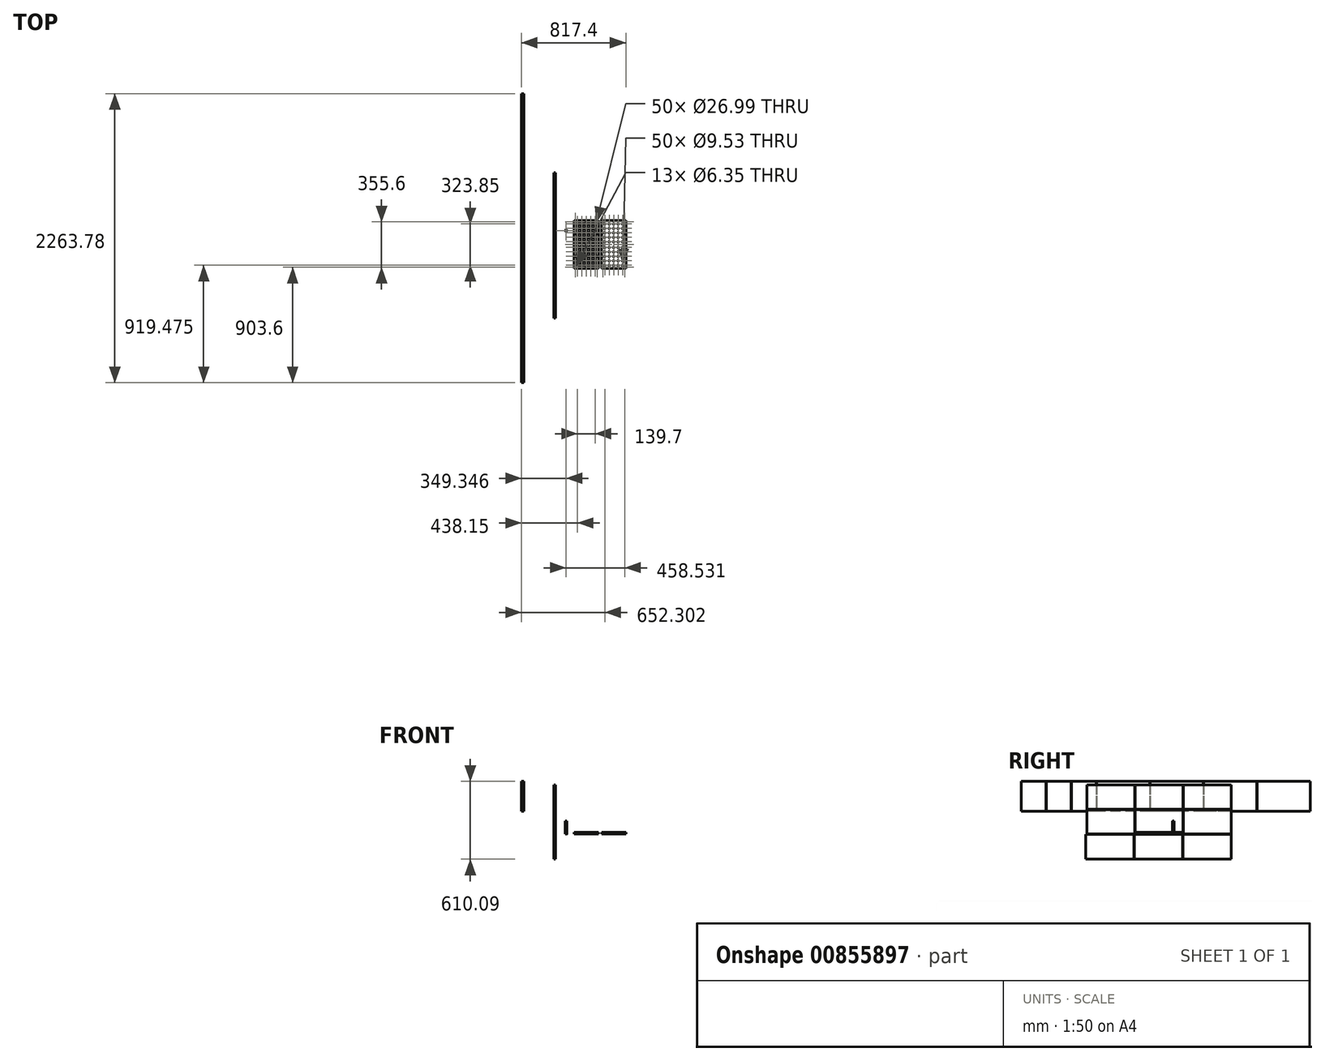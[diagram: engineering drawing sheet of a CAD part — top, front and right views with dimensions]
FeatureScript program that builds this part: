
annotation { "Feature Type Name" : "Feature", "Feature Type Description" : "" }
export const myFeature = defineFeature(function(context is Context, id is Id, definition is map)
    precondition{}
    {
        {
            var Q0;
            Q0=qCreatedBy(makeId("Top.planeOp"),FACE);
            var sketch = newSketch(context, id + "F0", { "sketchPlane" : qUnion([Q0])});
            skLineSegment(sketch, "E0.bottom", {"start": v(95.25, -187.33) * mm, "end": v(-95.25, -187.33) * mm});
            skLineSegment(sketch, "E0.top", {"start": v(95.25, 187.33) * mm, "end": v(-95.25, 187.33) * mm});
            skLineSegment(sketch, "E0.left", {"start": v(95.25, -187.33) * mm, "end": v(95.25, 187.33) * mm});
            skLineSegment(sketch, "E0.right", {"start": v(-95.25, -187.33) * mm, "end": v(-95.25, 187.33) * mm});
            skPoint(sketch, "E0.middle", {"position": v(0, 0) * mm});
            skSolve(sketch);
        }
        {
            var Q0;
            Q0=makeQuery(id+"F0.imprint","IMPRINT",FACE,{"disambiguationData":[TD([[makeQuery(id+"F0.imprint","IMPRINT",EDGE,{"derivedFrom":sQuery(id+"F0.wireOp",EDGE,"E0.bottom")}),-1.0]])]});
            extrude(context, id + "F1", {"entities" : qUnion([Q0]), "depth" : 12.7 * mm, "offsetDistance" : 25.4 * mm});
        }
        {
            var Q0;
            Q0=makeQuery(id+"F1.opExtrude","CAP_FACE",FACE,{"disambiguationData":[OSD([sQuery(id+"F0.wireOp",EDGE,"E0.bottom"),sQuery(id+"F0.wireOp",EDGE,"E0.top"),sQuery(id+"F0.wireOp",EDGE,"E0.left"),sQuery(id+"F0.wireOp",EDGE,"E0.right")])],"isStart":false});
            var sketch = newSketch(context, id + "F2", { "sketchPlane" : qUnion([Q0])});
            skLineSegment(sketch, "E1", {"start": v(-95.25, 161.92) * mm, "end": v(95.25, 161.93) * mm, "construction": true});
            skLineSegment(sketch, "E2", {"start": v(-69.85, 187.33) * mm, "end": v(-69.85, -187.33) * mm, "construction": true});
            skCircle(sketch, "E3", {"center": v(-69.85, 161.93) * mm, "radius": 13.5 * mm});
            skCircle(sketch, "E4.0.1.0", {"center": v(-69.85, 127) * mm, "radius": 13.5 * mm});
            skCircle(sketch, "E4.0.2.0", {"center": v(-69.85, 92.08) * mm, "radius": 13.5 * mm});
            skCircle(sketch, "E4.0.3.0", {"center": v(-69.85, 57.15) * mm, "radius": 13.5 * mm});
            skCircle(sketch, "E4.0.4.0", {"center": v(-69.85, 22.22) * mm, "radius": 13.5 * mm});
            skCircle(sketch, "E4.1.0.0", {"center": v(-34.93, 161.93) * mm, "radius": 13.5 * mm});
            skCircle(sketch, "E4.1.1.0", {"center": v(-34.93, 127) * mm, "radius": 13.5 * mm});
            skCircle(sketch, "E4.1.2.0", {"center": v(-34.93, 92.08) * mm, "radius": 13.5 * mm});
            skCircle(sketch, "E4.1.3.0", {"center": v(-34.93, 57.15) * mm, "radius": 13.5 * mm});
            skCircle(sketch, "E4.1.4.0", {"center": v(-34.93, 22.22) * mm, "radius": 13.5 * mm});
            skCircle(sketch, "E4.2.0.0", {"center": v(0, 161.93) * mm, "radius": 13.5 * mm});
            skCircle(sketch, "E4.2.1.0", {"center": v(0, 127) * mm, "radius": 13.5 * mm});
            skCircle(sketch, "E4.2.2.0", {"center": v(0, 92.08) * mm, "radius": 13.5 * mm});
            skCircle(sketch, "E4.2.3.0", {"center": v(0, 57.15) * mm, "radius": 13.5 * mm});
            skCircle(sketch, "E4.2.4.0", {"center": v(0, 22.22) * mm, "radius": 13.5 * mm});
            skCircle(sketch, "E4.3.0.0", {"center": v(34.92, 161.93) * mm, "radius": 13.5 * mm});
            skCircle(sketch, "E4.3.1.0", {"center": v(34.92, 127) * mm, "radius": 13.5 * mm});
            skCircle(sketch, "E4.3.2.0", {"center": v(34.92, 92.08) * mm, "radius": 13.5 * mm});
            skCircle(sketch, "E4.3.3.0", {"center": v(34.92, 57.15) * mm, "radius": 13.5 * mm});
            skCircle(sketch, "E4.3.4.0", {"center": v(34.92, 22.22) * mm, "radius": 13.5 * mm});
            skCircle(sketch, "E4.4.0.0", {"center": v(69.85, 161.93) * mm, "radius": 13.5 * mm});
            skCircle(sketch, "E4.4.1.0", {"center": v(69.85, 127) * mm, "radius": 13.5 * mm});
            skCircle(sketch, "E4.4.2.0", {"center": v(69.85, 92.08) * mm, "radius": 13.5 * mm});
            skCircle(sketch, "E4.4.3.0", {"center": v(69.85, 57.15) * mm, "radius": 13.5 * mm});
            skCircle(sketch, "E4.4.4.0", {"center": v(69.85, 22.22) * mm, "radius": 13.5 * mm});
            skLineSegment(sketch, "E4.direction1", {"start": v(-69.85, 161.93) * mm, "end": v(-34.93, 161.93) * mm, "construction": true});
            skLineSegment(sketch, "E4.direction2", {"start": v(-69.85, 161.93) * mm, "end": v(-69.85, 127) * mm, "construction": true});
            skLineSegment(sketch, "E5", {"start": v(-95.25, -161.93) * mm, "end": v(95.25, -161.92) * mm, "construction": true});
            skCircle(sketch, "E6", {"center": v(-69.85, -161.93) * mm, "radius": 13.5 * mm});
            skLineSegment(sketch, "E7", {"start": v(95.25, -177.8) * mm, "end": v(-95.25, -177.8) * mm, "construction": true});
            skLineSegment(sketch, "E8", {"start": v(85.73, -187.33) * mm, "end": v(85.73, 187.33) * mm, "construction": true});
            skLineSegment(sketch, "E9", {"start": v(-95.25, 0) * mm, "end": v(95.25, 0) * mm, "construction": true});
            skLineSegment(sketch, "E10", {"start": v(-95.25, 177.8) * mm, "end": v(95.25, 177.8) * mm, "construction": true});
            skLineSegment(sketch, "E11", {"start": v(-85.73, 187.33) * mm, "end": v(-85.72, -187.33) * mm, "construction": true});
            skCircle(sketch, "E12", {"center": v(-85.73, 177.8) * mm, "radius": 3.18 * mm});
            skCircle(sketch, "E13", {"center": v(85.73, 177.8) * mm, "radius": 3.18 * mm});
            skCircle(sketch, "E14", {"center": v(-85.73, 0) * mm, "radius": 3.18 * mm});
            skCircle(sketch, "E15", {"center": v(85.73, 0) * mm, "radius": 3.18 * mm});
            skCircle(sketch, "E16", {"center": v(-85.72, -177.8) * mm, "radius": 3.18 * mm});
            skCircle(sketch, "E17", {"center": v(85.73, -177.8) * mm, "radius": 3.18 * mm});
            skCircle(sketch, "E18.0.1.0", {"center": v(-69.85, -127) * mm, "radius": 13.5 * mm});
            skCircle(sketch, "E18.0.2.0", {"center": v(-69.85, -92.08) * mm, "radius": 13.5 * mm});
            skCircle(sketch, "E18.0.3.0", {"center": v(-69.85, -57.15) * mm, "radius": 13.5 * mm});
            skCircle(sketch, "E18.0.4.0", {"center": v(-69.85, -22.23) * mm, "radius": 13.5 * mm});
            skCircle(sketch, "E18.1.0.0", {"center": v(-34.93, -161.93) * mm, "radius": 13.5 * mm});
            skCircle(sketch, "E18.1.1.0", {"center": v(-34.93, -127) * mm, "radius": 13.5 * mm});
            skCircle(sketch, "E18.1.2.0", {"center": v(-34.93, -92.08) * mm, "radius": 13.5 * mm});
            skCircle(sketch, "E18.1.3.0", {"center": v(-34.93, -57.15) * mm, "radius": 13.5 * mm});
            skCircle(sketch, "E18.1.4.0", {"center": v(-34.93, -22.23) * mm, "radius": 13.5 * mm});
            skCircle(sketch, "E18.2.0.0", {"center": v(0, -161.93) * mm, "radius": 13.5 * mm});
            skCircle(sketch, "E18.2.1.0", {"center": v(0, -127) * mm, "radius": 13.5 * mm});
            skCircle(sketch, "E18.2.2.0", {"center": v(0, -92.08) * mm, "radius": 13.5 * mm});
            skCircle(sketch, "E18.2.3.0", {"center": v(0, -57.15) * mm, "radius": 13.5 * mm});
            skCircle(sketch, "E18.2.4.0", {"center": v(0, -22.23) * mm, "radius": 13.5 * mm});
            skCircle(sketch, "E18.3.0.0", {"center": v(34.92, -161.93) * mm, "radius": 13.5 * mm});
            skCircle(sketch, "E18.3.1.0", {"center": v(34.92, -127) * mm, "radius": 13.5 * mm});
            skCircle(sketch, "E18.3.2.0", {"center": v(34.92, -92.08) * mm, "radius": 13.5 * mm});
            skCircle(sketch, "E18.3.3.0", {"center": v(34.92, -57.15) * mm, "radius": 13.5 * mm});
            skCircle(sketch, "E18.3.4.0", {"center": v(34.92, -22.23) * mm, "radius": 13.5 * mm});
            skCircle(sketch, "E18.4.0.0", {"center": v(69.85, -161.93) * mm, "radius": 13.5 * mm});
            skCircle(sketch, "E18.4.1.0", {"center": v(69.85, -127) * mm, "radius": 13.5 * mm});
            skCircle(sketch, "E18.4.2.0", {"center": v(69.85, -92.08) * mm, "radius": 13.5 * mm});
            skCircle(sketch, "E18.4.3.0", {"center": v(69.85, -57.15) * mm, "radius": 13.5 * mm});
            skCircle(sketch, "E18.4.4.0", {"center": v(69.85, -22.23) * mm, "radius": 13.5 * mm});
            skLineSegment(sketch, "E18.direction1", {"start": v(-69.85, -161.93) * mm, "end": v(-34.93, -161.93) * mm, "construction": true});
            skLineSegment(sketch, "E18.direction2", {"start": v(-69.85, -161.93) * mm, "end": v(-69.85, -127) * mm, "construction": true});
            skSolve(sketch);
        }
        {
            var Q0;
            Q0 = qSketchRegion(id + "F2", true);
            extrude(context, id + "F3", {"entities" : qUnion([Q0]), "operationType" : NewBodyOperationType.REMOVE, "endBound" : BoundingType.UP_TO_NEXT, "oppositeDirection" : true, "depth" : 25.4 * mm, "offsetDistance" : 25.4 * mm});
        }
        {
            var Q0;
            Q0=qCreatedBy(makeId("Top.planeOp"),FACE);
            var sketch = newSketch(context, id + "F4", { "sketchPlane" : qUnion([Q0])});
            skCircle(sketch, "E19", {"center": v(-158.65, 110) * mm, "radius": 6.35 * mm});
            skCircle(sketch, "E20", {"center": v(-158.65, 110) * mm, "radius": 3.18 * mm});
            skSolve(sketch);
        }
        {
            var Q0;
            Q0=makeQuery(id+"F4.imprint","IMPRINT",FACE,{"disambiguationData":[TD([[makeQuery(id+"F4.imprint","IMPRINT",EDGE,{"derivedFrom":sQuery(id+"F4.wireOp",EDGE,"E19")}),1.0]])]});
            extrude(context, id + "F5", {"entities" : qUnion([Q0]), "depth" : 101.6 * mm, "offsetDistance" : 25.4 * mm});
        }
        {
            var Q0;
            Q0=qCreatedBy(makeId("Top.planeOp"),FACE);
            var sketch = newSketch(context, id + "F6", { "sketchPlane" : qUnion([Q0])});
            skLineSegment(sketch, "E21.bottom", {"start": v(118.9, 187.33) * mm, "end": v(309.4, 187.33) * mm});
            skLineSegment(sketch, "E21.top", {"start": v(118.9, -187.33) * mm, "end": v(309.4, -187.33) * mm});
            skLineSegment(sketch, "E21.left", {"start": v(118.9, 187.33) * mm, "end": v(118.9, -187.33) * mm});
            skLineSegment(sketch, "E21.right", {"start": v(309.4, 187.33) * mm, "end": v(309.4, -187.33) * mm});
            skPoint(sketch, "E21.middle", {"position": v(214.15, 0) * mm});
            skSolve(sketch);
        }
        {
            var Q0;
            Q0=makeQuery(id+"F6.imprint","IMPRINT",FACE,{"disambiguationData":[TD([[makeQuery(id+"F6.imprint","IMPRINT",EDGE,{"derivedFrom":sQuery(id+"F6.wireOp",EDGE,"E21.bottom")}),-1.0]])]});
            extrude(context, id + "F7", {"entities" : qUnion([Q0]), "depth" : 12.7 * mm, "offsetDistance" : 25.4 * mm});
        }
        {
            var Q0;
            Q0=makeQuery(id+"F7.opExtrude","CAP_FACE",FACE,{"disambiguationData":[OSD([sQuery(id+"F6.wireOp",EDGE,"E21.bottom"),sQuery(id+"F6.wireOp",EDGE,"E21.top"),sQuery(id+"F6.wireOp",EDGE,"E21.left"),sQuery(id+"F6.wireOp",EDGE,"E21.right")])],"isStart":false});
            var sketch = newSketch(context, id + "F8", { "sketchPlane" : qUnion([Q0])});
            skLineSegment(sketch, "E22", {"start": v(118.9, 177.8) * mm, "end": v(309.4, 177.8) * mm, "construction": true});
            skLineSegment(sketch, "E23", {"start": v(118.9, -177.8) * mm, "end": v(309.4, -177.8) * mm, "construction": true});
            skLineSegment(sketch, "E24", {"start": v(128.43, 187.33) * mm, "end": v(128.43, -187.33) * mm, "construction": true});
            skLineSegment(sketch, "E25", {"start": v(299.88, 187.33) * mm, "end": v(299.88, -187.33) * mm, "construction": true});
            skLineSegment(sketch, "E26", {"start": v(118.9, 0) * mm, "end": v(309.4, 0) * mm, "construction": true});
            skCircle(sketch, "E27", {"center": v(128.43, 177.8) * mm, "radius": 3.18 * mm});
            skCircle(sketch, "E28", {"center": v(299.88, 177.8) * mm, "radius": 3.18 * mm});
            skCircle(sketch, "E29", {"center": v(128.43, 0) * mm, "radius": 3.18 * mm});
            skCircle(sketch, "E30", {"center": v(299.88, 0) * mm, "radius": 3.18 * mm});
            skCircle(sketch, "E31", {"center": v(128.43, -177.8) * mm, "radius": 3.17 * mm});
            skCircle(sketch, "E32", {"center": v(299.88, -177.8) * mm, "radius": 3.18 * mm});
            skSolve(sketch);
        }
        {
            var Q0;
            Q0 = qSketchRegion(id + "F8", true);
            extrude(context, id + "F9", {"entities" : qUnion([Q0]), "operationType" : NewBodyOperationType.REMOVE, "oppositeDirection" : true, "depth" : 25.4 * mm, "offsetDistance" : 25.4 * mm});
        }
        {
            var Q0;
            Q0=makeQuery(id+"F7.opExtrude","CAP_FACE",FACE,{"disambiguationData":[OSD([sQuery(id+"F6.wireOp",EDGE,"E21.bottom"),sQuery(id+"F6.wireOp",EDGE,"E21.top"),sQuery(id+"F6.wireOp",EDGE,"E21.left"),sQuery(id+"F6.wireOp",EDGE,"E21.right")])],"isStart":false});
            var sketch = newSketch(context, id + "F10", { "sketchPlane" : qUnion([Q0])});
            skLineSegment(sketch, "E33", {"start": v(144.3, 187.33) * mm, "end": v(144.3, -187.33) * mm, "construction": true});
            skLineSegment(sketch, "E34", {"start": v(118.9, 161.93) * mm, "end": v(309.4, 161.93) * mm, "construction": true});
            skLineSegment(sketch, "E35", {"start": v(118.9, -161.92) * mm, "end": v(309.4, -161.92) * mm, "construction": true});
            skCircle(sketch, "E36", {"center": v(144.3, 161.92) * mm, "radius": 4.76 * mm});
            skCircle(sketch, "E37.0.1.0", {"center": v(144.3, 127) * mm, "radius": 4.76 * mm});
            skCircle(sketch, "E37.0.2.0", {"center": v(144.3, 92.07) * mm, "radius": 4.76 * mm});
            skCircle(sketch, "E37.0.3.0", {"center": v(144.3, 57.15) * mm, "radius": 4.76 * mm});
            skCircle(sketch, "E37.0.4.0", {"center": v(144.3, 22.22) * mm, "radius": 4.76 * mm});
            skCircle(sketch, "E37.1.0.0", {"center": v(179.23, 161.92) * mm, "radius": 4.76 * mm});
            skCircle(sketch, "E37.1.1.0", {"center": v(179.23, 127) * mm, "radius": 4.76 * mm});
            skCircle(sketch, "E37.1.2.0", {"center": v(179.23, 92.07) * mm, "radius": 4.76 * mm});
            skCircle(sketch, "E37.1.3.0", {"center": v(179.23, 57.15) * mm, "radius": 4.76 * mm});
            skCircle(sketch, "E37.1.4.0", {"center": v(179.23, 22.22) * mm, "radius": 4.76 * mm});
            skCircle(sketch, "E37.2.0.0", {"center": v(214.15, 161.92) * mm, "radius": 4.76 * mm});
            skCircle(sketch, "E37.2.1.0", {"center": v(214.15, 127) * mm, "radius": 4.76 * mm});
            skCircle(sketch, "E37.2.2.0", {"center": v(214.15, 92.07) * mm, "radius": 4.76 * mm});
            skCircle(sketch, "E37.2.3.0", {"center": v(214.15, 57.15) * mm, "radius": 4.76 * mm});
            skCircle(sketch, "E37.2.4.0", {"center": v(214.15, 22.22) * mm, "radius": 4.76 * mm});
            skCircle(sketch, "E37.3.0.0", {"center": v(249.08, 161.92) * mm, "radius": 4.76 * mm});
            skCircle(sketch, "E37.3.1.0", {"center": v(249.08, 127) * mm, "radius": 4.76 * mm});
            skCircle(sketch, "E37.3.2.0", {"center": v(249.08, 92.07) * mm, "radius": 4.76 * mm});
            skCircle(sketch, "E37.3.3.0", {"center": v(249.08, 57.15) * mm, "radius": 4.76 * mm});
            skCircle(sketch, "E37.3.4.0", {"center": v(249.08, 22.22) * mm, "radius": 4.76 * mm});
            skCircle(sketch, "E37.4.0.0", {"center": v(284, 161.92) * mm, "radius": 4.76 * mm});
            skCircle(sketch, "E37.4.1.0", {"center": v(284, 127) * mm, "radius": 4.76 * mm});
            skCircle(sketch, "E37.4.2.0", {"center": v(284, 92.07) * mm, "radius": 4.76 * mm});
            skCircle(sketch, "E37.4.3.0", {"center": v(284, 57.15) * mm, "radius": 4.76 * mm});
            skCircle(sketch, "E37.4.4.0", {"center": v(284, 22.22) * mm, "radius": 4.76 * mm});
            skLineSegment(sketch, "E37.direction1", {"start": v(144.3, 161.93) * mm, "end": v(179.23, 161.93) * mm, "construction": true});
            skLineSegment(sketch, "E37.direction2", {"start": v(144.3, 161.92) * mm, "end": v(144.3, 127) * mm, "construction": true});
            skCircle(sketch, "E38", {"center": v(144.3, -161.92) * mm, "radius": 4.76 * mm});
            skCircle(sketch, "E39.0.1.0", {"center": v(144.3, -127) * mm, "radius": 4.76 * mm});
            skCircle(sketch, "E39.0.2.0", {"center": v(144.3, -92.07) * mm, "radius": 4.76 * mm});
            skCircle(sketch, "E39.0.3.0", {"center": v(144.3, -57.15) * mm, "radius": 4.76 * mm});
            skCircle(sketch, "E39.0.4.0", {"center": v(144.3, -22.22) * mm, "radius": 4.76 * mm});
            skCircle(sketch, "E39.1.0.0", {"center": v(179.23, -161.92) * mm, "radius": 4.76 * mm});
            skCircle(sketch, "E39.1.1.0", {"center": v(179.23, -127) * mm, "radius": 4.76 * mm});
            skCircle(sketch, "E39.1.2.0", {"center": v(179.23, -92.07) * mm, "radius": 4.76 * mm});
            skCircle(sketch, "E39.1.3.0", {"center": v(179.23, -57.15) * mm, "radius": 4.76 * mm});
            skCircle(sketch, "E39.1.4.0", {"center": v(179.23, -22.22) * mm, "radius": 4.76 * mm});
            skCircle(sketch, "E39.2.0.0", {"center": v(214.15, -161.92) * mm, "radius": 4.76 * mm});
            skCircle(sketch, "E39.2.1.0", {"center": v(214.15, -127) * mm, "radius": 4.76 * mm});
            skCircle(sketch, "E39.2.2.0", {"center": v(214.15, -92.07) * mm, "radius": 4.76 * mm});
            skCircle(sketch, "E39.2.3.0", {"center": v(214.15, -57.15) * mm, "radius": 4.76 * mm});
            skCircle(sketch, "E39.2.4.0", {"center": v(214.15, -22.22) * mm, "radius": 4.76 * mm});
            skCircle(sketch, "E39.3.0.0", {"center": v(249.08, -161.92) * mm, "radius": 4.76 * mm});
            skCircle(sketch, "E39.3.1.0", {"center": v(249.08, -127) * mm, "radius": 4.76 * mm});
            skCircle(sketch, "E39.3.2.0", {"center": v(249.08, -92.07) * mm, "radius": 4.76 * mm});
            skCircle(sketch, "E39.3.3.0", {"center": v(249.08, -57.15) * mm, "radius": 4.76 * mm});
            skCircle(sketch, "E39.3.4.0", {"center": v(249.08, -22.22) * mm, "radius": 4.76 * mm});
            skCircle(sketch, "E39.4.0.0", {"center": v(284, -161.92) * mm, "radius": 4.76 * mm});
            skCircle(sketch, "E39.4.1.0", {"center": v(284, -127) * mm, "radius": 4.76 * mm});
            skCircle(sketch, "E39.4.2.0", {"center": v(284, -92.07) * mm, "radius": 4.76 * mm});
            skCircle(sketch, "E39.4.3.0", {"center": v(284, -57.15) * mm, "radius": 4.76 * mm});
            skCircle(sketch, "E39.4.4.0", {"center": v(284, -22.22) * mm, "radius": 4.76 * mm});
            skLineSegment(sketch, "E39.direction1", {"start": v(144.3, -161.92) * mm, "end": v(179.23, -161.92) * mm, "construction": true});
            skLineSegment(sketch, "E39.direction2", {"start": v(144.3, -161.92) * mm, "end": v(144.3, -127) * mm, "construction": true});
            skSolve(sketch);
        }
        {
            var Q0;
            Q0 = qSketchRegion(id + "F10", true);
            extrude(context, id + "F11", {"entities" : qUnion([Q0]), "operationType" : NewBodyOperationType.REMOVE, "oppositeDirection" : true, "depth" : 12.7 * mm, "offsetDistance" : 25.4 * mm});
        }
        {
            var Q0;
            Q0=qCreatedBy(makeId("Right.planeOp"),FACE);
            cPlane(context, id + "F12", {"entities" : qUnion([Q0]), "cplaneType" : CPlaneType.OFFSET, "offset" : 254 * mm, "oppositeDirection" : true, "width" : 152.4 * mm, "height" : 152.4 * mm});
        }
        {
            var Q0;
            Q0=qCreatedBy(id+"F12.planeOp",FACE);
            var sketch = newSketch(context, id + "F13", { "sketchPlane" : qUnion([Q0])});
            skLineSegment(sketch, "E40.bottom", {"start": v(-655.75, 384.17) * mm, "end": v(563.45, 384.18) * mm});
            skLineSegment(sketch, "E40.top", {"start": v(-655.75, -225.43) * mm, "end": v(563.45, -225.42) * mm});
            skLineSegment(sketch, "E40.left", {"start": v(-655.75, 384.17) * mm, "end": v(-655.75, -225.43) * mm});
            skLineSegment(sketch, "E40.right", {"start": v(563.45, 384.18) * mm, "end": v(563.45, -225.42) * mm});
            skLineSegment(sketch, "E41", {"start": v(563.45, 193.68) * mm, "end": v(-655.75, 193.67) * mm});
            skLineSegment(sketch, "E42", {"start": v(563.45, 190.5) * mm, "end": v(-655.75, 190.5) * mm});
            skLineSegment(sketch, "E43", {"start": v(563.45, 0) * mm, "end": v(-655.75, 0) * mm});
            skLineSegment(sketch, "E44", {"start": v(563.45, -3.18) * mm, "end": v(-655.75, -3.18) * mm});
            skLineSegment(sketch, "E45", {"start": v(563.45, -196.85) * mm, "end": v(-655.75, -196.85) * mm});
            skLineSegment(sketch, "E46", {"start": v(188.8, 384.18) * mm, "end": v(188.8, 0) * mm});
            skLineSegment(sketch, "E47", {"start": v(185.63, 384.18) * mm, "end": v(185.63, 0) * mm});
            skLineSegment(sketch, "E48", {"start": v(-189.02, 384.17) * mm, "end": v(-189.02, 0) * mm});
            skLineSegment(sketch, "E49", {"start": v(-192.2, 384.17) * mm, "end": v(-192.2, 0) * mm});
            skLineSegment(sketch, "E50", {"start": v(-566.85, 384.17) * mm, "end": v(-566.85, 0) * mm});
            skLineSegment(sketch, "E51", {"start": v(185.63, -3.17) * mm, "end": v(185.63, -196.85) * mm});
            skLineSegment(sketch, "E52", {"start": v(182.45, -3.17) * mm, "end": v(182.45, -196.85) * mm});
            skLineSegment(sketch, "E53", {"start": v(-195.37, -3.18) * mm, "end": v(-195.37, -196.85) * mm});
            skLineSegment(sketch, "E54", {"start": v(-198.55, -3.18) * mm, "end": v(-198.55, -196.85) * mm});
            skLineSegment(sketch, "E55", {"start": v(-576.37, -3.18) * mm, "end": v(-576.37, -196.85) * mm});
            skSolve(sketch);
        }
        {
            var Q0;
            {var subQ0=sQuery(id+"F13.wireOp",EDGE,"E52");Q0=makeQuery(id+"F13.imprint","IMPRINT",FACE,{"disambiguationData":[TD([[makeQuery(id+"F13.imprint","IMPRINT",EDGE,{"derivedFrom":subQ0}),-1.0]])]});}
            cPlane(context, id + "F14", {"entities" : qUnion([Q0]), "cplaneType" : CPlaneType.OFFSET, "offset" : 254 * mm, "oppositeDirection" : true, "width" : 152.4 * mm, "height" : 152.4 * mm});
        }
        {
            var Q0;
            Q0=qCreatedBy(id+"F14.planeOp",FACE);
            var sketch = newSketch(context, id + "F15", { "sketchPlane" : qUnion([Q0])});
            skLineSegment(sketch, "E56.bottom", {"start": v(1182.38, 413.24) * mm, "end": v(-1256.02, 413.24) * mm});
            skLineSegment(sketch, "E56.top", {"start": v(1182.38, 178.3) * mm, "end": v(-1256.02, 178.3) * mm});
            skLineSegment(sketch, "E56.left", {"start": v(1182.38, 413.24) * mm, "end": v(1182.38, 178.3) * mm});
            skLineSegment(sketch, "E56.right", {"start": v(-1256.02, 413.24) * mm, "end": v(-1256.02, 178.3) * mm});
            skLineSegment(sketch, "E57", {"start": v(766.45, 413.24) * mm, "end": v(766.45, 178.3) * mm});
            skLineSegment(sketch, "E58", {"start": v(763.28, 413.24) * mm, "end": v(763.28, 178.3) * mm});
            skLineSegment(sketch, "E59", {"start": v(347.35, 413.24) * mm, "end": v(347.35, 178.3) * mm});
            skLineSegment(sketch, "E60", {"start": v(344.18, 413.24) * mm, "end": v(344.18, 178.3) * mm});
            skLineSegment(sketch, "E61", {"start": v(-71.75, 413.24) * mm, "end": v(-71.75, 178.3) * mm});
            skLineSegment(sketch, "E62", {"start": v(-74.92, 413.24) * mm, "end": v(-74.92, 178.3) * mm});
            skLineSegment(sketch, "E63", {"start": v(-490.85, 413.24) * mm, "end": v(-490.85, 178.3) * mm});
            skLineSegment(sketch, "E64", {"start": v(-494.02, 413.24) * mm, "end": v(-494.02, 178.3) * mm});
            skLineSegment(sketch, "E65", {"start": v(-687.7, 413.24) * mm, "end": v(-687.7, 178.3) * mm});
            skLineSegment(sketch, "E66", {"start": v(-690.87, 413.24) * mm, "end": v(-690.87, 178.3) * mm});
            skLineSegment(sketch, "E67", {"start": v(-884.55, 413.24) * mm, "end": v(-884.55, 178.3) * mm});
            skLineSegment(sketch, "E68", {"start": v(-887.72, 413.24) * mm, "end": v(-887.72, 178.3) * mm});
            skLineSegment(sketch, "E69", {"start": v(-1081.4, 413.24) * mm, "end": v(-1081.4, 178.3) * mm});
            skSolve(sketch);
        }
        {
            var Q0;
            {var subQ0=sQuery(id+"F15.wireOp",EDGE,"E56.left");Q0=makeQuery(id+"F15.imprint","IMPRINT",FACE,{"disambiguationData":[TD([[makeQuery(id+"F15.imprint","IMPRINT",EDGE,{"derivedFrom":subQ0}),-1.0]])]});}
            var Q1;
            {var subQ0=sQuery(id+"F15.wireOp",EDGE,"E58");Q1=makeQuery(id+"F15.imprint","IMPRINT",FACE,{"disambiguationData":[TD([[makeQuery(id+"F15.imprint","IMPRINT",EDGE,{"derivedFrom":subQ0}),-1.0]])]});}
            var Q2;
            {var subQ0=sQuery(id+"F15.wireOp",EDGE,"E60");Q2=makeQuery(id+"F15.imprint","IMPRINT",FACE,{"disambiguationData":[TD([[makeQuery(id+"F15.imprint","IMPRINT",EDGE,{"derivedFrom":subQ0}),-1.0]])]});}
            var Q3;
            {var subQ0=sQuery(id+"F15.wireOp",EDGE,"E62");Q3=makeQuery(id+"F15.imprint","IMPRINT",FACE,{"disambiguationData":[TD([[makeQuery(id+"F15.imprint","IMPRINT",EDGE,{"derivedFrom":subQ0}),-1.0]])]});}
            var Q4;
            {var subQ0=sQuery(id+"F15.wireOp",EDGE,"E64");Q4=makeQuery(id+"F15.imprint","IMPRINT",FACE,{"disambiguationData":[TD([[makeQuery(id+"F15.imprint","IMPRINT",EDGE,{"derivedFrom":subQ0}),-1.0]])]});}
            var Q5;
            {var subQ0=sQuery(id+"F15.wireOp",EDGE,"E66");Q5=makeQuery(id+"F15.imprint","IMPRINT",FACE,{"disambiguationData":[TD([[makeQuery(id+"F15.imprint","IMPRINT",EDGE,{"derivedFrom":subQ0}),-1.0]])]});}
            var Q6;
            {var subQ0=sQuery(id+"F15.wireOp",EDGE,"E68");Q6=makeQuery(id+"F15.imprint","IMPRINT",FACE,{"disambiguationData":[TD([[makeQuery(id+"F15.imprint","IMPRINT",EDGE,{"derivedFrom":subQ0}),-1.0]])]});}
            extrude(context, id + "F16", {"entities" : qUnion([Q0, Q1, Q2, Q3, Q4, Q5, Q6]), "depth" : 19.05 * mm, "offsetDistance" : 25.4 * mm});
        }
        {
            var Q0;
            {var subQ0=sQuery(id+"F13.wireOp",EDGE,"E40.right");var subQ1=sQuery(id+"F13.wireOp",EDGE,"E40.bottom");var subQ2=makeQuery(id+"F13.imprint","INTERSECT",VERTEX,{"derivedFrom":[subQ1,subQ0]});Q0=makeQuery(id+"F13.imprint","IMPRINT",FACE,{"disambiguationData":[TD([[makeQuery(id+"F13.imprint","IMPRINT",EDGE,{"disambiguationData":[TD([[subQ2,1.0]])],"derivedFrom":subQ1}),-1.0]])]});}
            var Q1;
            {var subQ0=sQuery(id+"F13.wireOp",EDGE,"E47");var subQ1=sQuery(id+"F13.wireOp",EDGE,"E40.bottom");var subQ2=makeQuery(id+"F13.imprint","INTERSECT",VERTEX,{"derivedFrom":[subQ1,subQ0]});Q1=makeQuery(id+"F13.imprint","IMPRINT",FACE,{"disambiguationData":[TD([[makeQuery(id+"F13.imprint","IMPRINT",EDGE,{"disambiguationData":[TD([[subQ2,1.0]])],"derivedFrom":subQ1}),-1.0]])]});}
            var Q2;
            {var subQ0=sQuery(id+"F13.wireOp",EDGE,"E49");var subQ1=sQuery(id+"F13.wireOp",EDGE,"E40.bottom");var subQ2=makeQuery(id+"F13.imprint","INTERSECT",VERTEX,{"derivedFrom":[subQ1,subQ0]});Q2=makeQuery(id+"F13.imprint","IMPRINT",FACE,{"disambiguationData":[TD([[makeQuery(id+"F13.imprint","IMPRINT",EDGE,{"disambiguationData":[TD([[subQ2,1.0]])],"derivedFrom":subQ1}),-1.0]])]});}
            var Q3;
            {var subQ0=sQuery(id+"F13.wireOp",EDGE,"E42");var subQ1=sQuery(id+"F13.wireOp",EDGE,"E40.right");var subQ2=makeQuery(id+"F13.imprint","INTERSECT",VERTEX,{"derivedFrom":[subQ1,subQ0]});Q3=makeQuery(id+"F13.imprint","IMPRINT",FACE,{"disambiguationData":[TD([[makeQuery(id+"F13.imprint","IMPRINT",EDGE,{"disambiguationData":[TD([[subQ2,-1.0]])],"derivedFrom":subQ1}),-1.0]])]});}
            var Q4;
            {var subQ0=sQuery(id+"F13.wireOp",EDGE,"E47");var subQ1=sQuery(id+"F13.wireOp",EDGE,"E42");var subQ2=makeQuery(id+"F13.imprint","INTERSECT",VERTEX,{"derivedFrom":[subQ1,subQ0]});Q4=makeQuery(id+"F13.imprint","IMPRINT",FACE,{"disambiguationData":[TD([[makeQuery(id+"F13.imprint","IMPRINT",EDGE,{"disambiguationData":[TD([[subQ2,-1.0]])],"derivedFrom":subQ1}),1.0]])]});}
            var Q5;
            {var subQ0=sQuery(id+"F13.wireOp",EDGE,"E49");var subQ1=sQuery(id+"F13.wireOp",EDGE,"E42");var subQ2=makeQuery(id+"F13.imprint","INTERSECT",VERTEX,{"derivedFrom":[subQ1,subQ0]});Q5=makeQuery(id+"F13.imprint","IMPRINT",FACE,{"disambiguationData":[TD([[makeQuery(id+"F13.imprint","IMPRINT",EDGE,{"disambiguationData":[TD([[subQ2,-1.0]])],"derivedFrom":subQ1}),1.0]])]});}
            var Q6;
            {var subQ5=sQuery(id+"F13.wireOp",EDGE,"E51");Q6=makeQuery(id+"F13.imprint","IMPRINT",FACE,{"disambiguationData":[TD([[makeQuery(id+"F13.imprint","IMPRINT",EDGE,{"derivedFrom":subQ5}),1.0]])]});}
            var Q7;
            {var subQ0=sQuery(id+"F13.wireOp",EDGE,"E52");Q7=makeQuery(id+"F13.imprint","IMPRINT",FACE,{"disambiguationData":[TD([[makeQuery(id+"F13.imprint","IMPRINT",EDGE,{"derivedFrom":subQ0}),-1.0]])]});}
            var Q8;
            {var subQ0=sQuery(id+"F13.wireOp",EDGE,"E54");Q8=makeQuery(id+"F13.imprint","IMPRINT",FACE,{"disambiguationData":[TD([[makeQuery(id+"F13.imprint","IMPRINT",EDGE,{"derivedFrom":subQ0}),-1.0]])]});}
            extrude(context, id + "F17", {"entities" : qUnion([Q0, Q1, Q2, Q3, Q4, Q5, Q6, Q7, Q8]), "depth" : 12.7 * mm, "offsetDistance" : 25.4 * mm});
        }
    });
